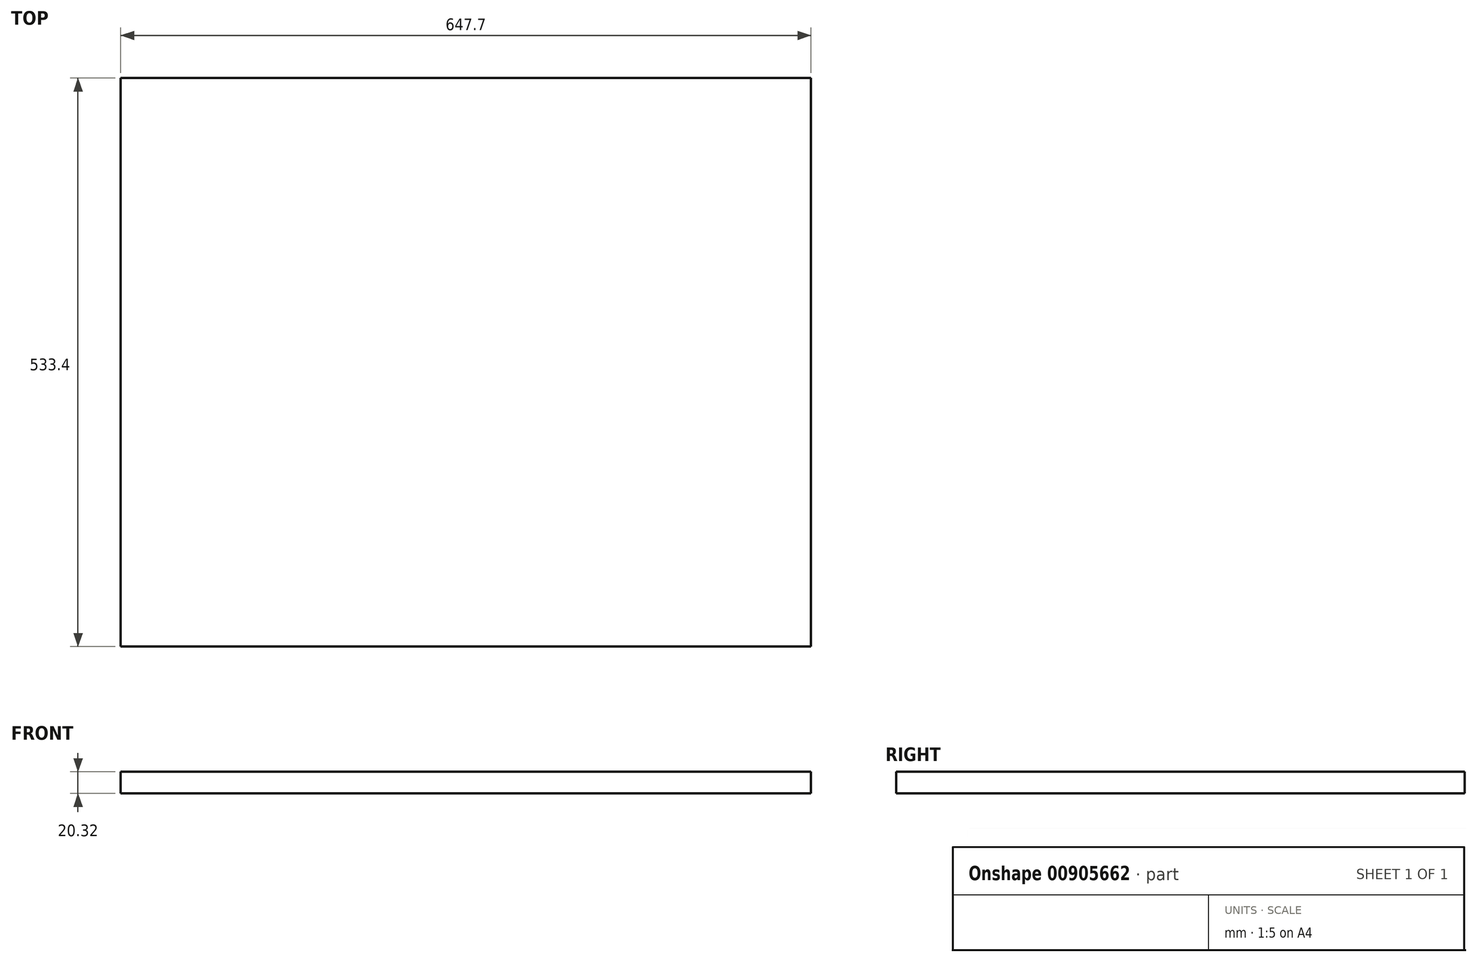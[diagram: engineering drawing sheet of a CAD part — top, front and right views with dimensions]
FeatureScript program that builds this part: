
annotation { "Feature Type Name" : "Feature", "Feature Type Description" : "" }
export const myFeature = defineFeature(function(context is Context, id is Id, definition is map)
    precondition{}
    {
        {
            var Q0;
            Q0=qCreatedBy(makeId("Top.planeOp"),FACE);
            var sketch = newSketch(context, id + "F0", { "sketchPlane" : qUnion([Q0])});
            skLineSegment(sketch, "E0.bottom", {"start": v(323.85, -266.7) * mm, "end": v(-323.85, -266.7) * mm});
            skLineSegment(sketch, "E0.top", {"start": v(323.85, 266.7) * mm, "end": v(-323.85, 266.7) * mm});
            skLineSegment(sketch, "E0.left", {"start": v(323.85, -266.7) * mm, "end": v(323.85, 266.7) * mm});
            skLineSegment(sketch, "E0.right", {"start": v(-323.85, -266.7) * mm, "end": v(-323.85, 266.7) * mm});
            skPoint(sketch, "E0.middle", {"position": v(0, 0) * mm});
            skSolve(sketch);
        }
        {
            var Q0;
            Q0=makeQuery(id+"F0.imprint","IMPRINT",FACE,{"disambiguationData":[TD([[makeQuery(id+"F0.imprint","IMPRINT",EDGE,{"derivedFrom":sQuery(id+"F0.wireOp",EDGE,"E0.bottom")}),-1.0]])]});
            extrude(context, id + "F1", {"entities" : qUnion([Q0]), "depth" : 20.32 * mm, "offsetDistance" : 25.4 * mm});
        }
    });
